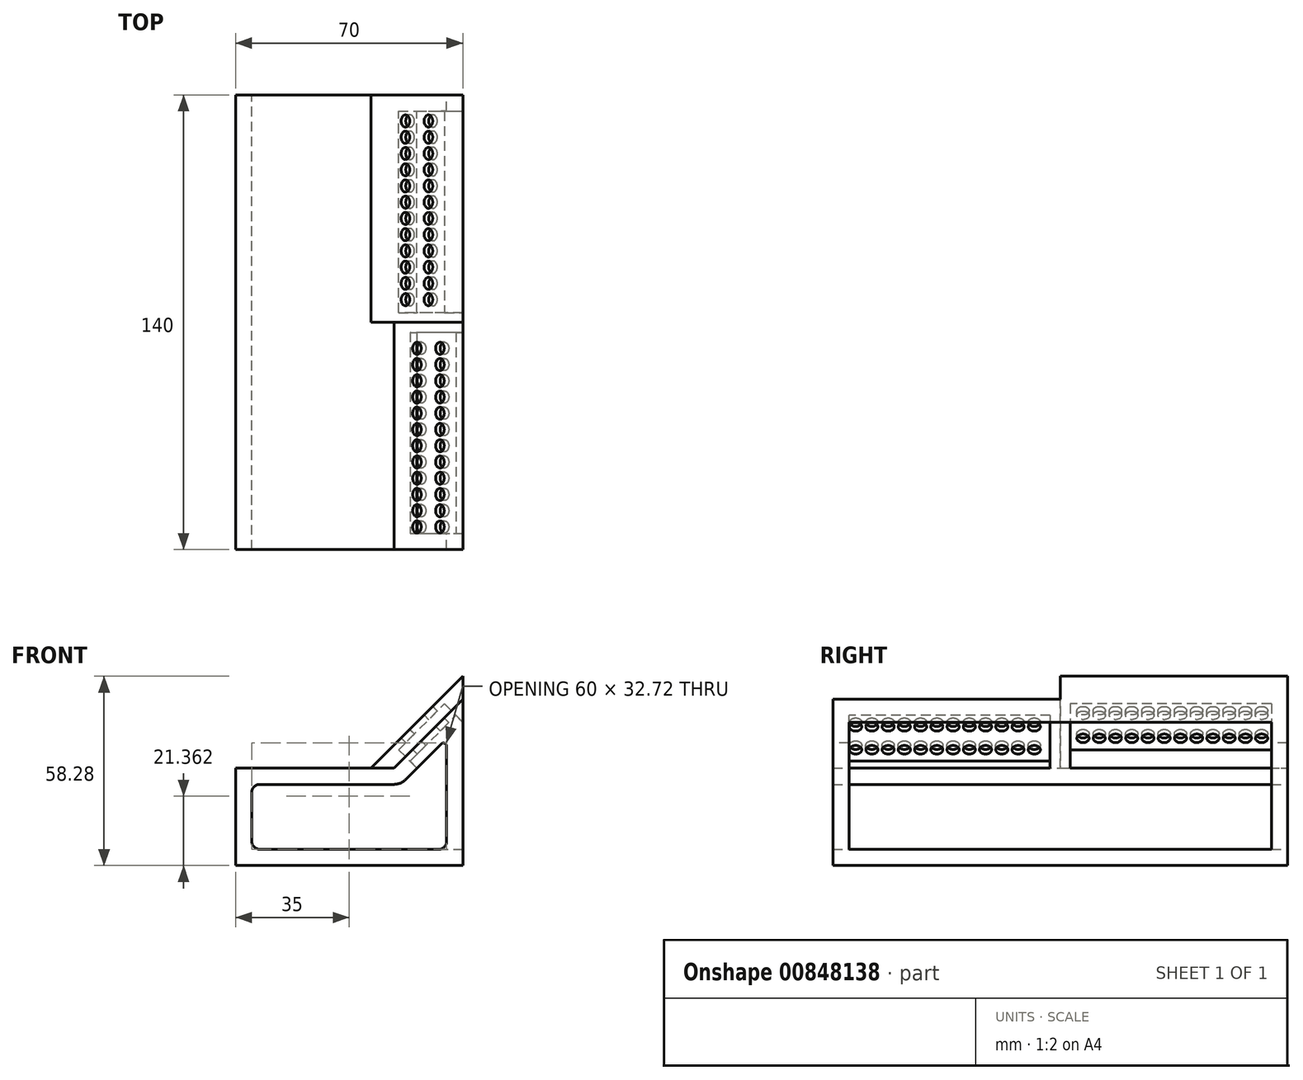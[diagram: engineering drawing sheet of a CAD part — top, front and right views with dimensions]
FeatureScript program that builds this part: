
annotation { "Feature Type Name" : "Feature", "Feature Type Description" : "" }
export const myFeature = defineFeature(function(context is Context, id is Id, definition is map)
    precondition{}
    {
        {
            var Q0;
            Q0=qCreatedBy(makeId("Front.planeOp"),FACE);
            var sketch = newSketch(context, id + "F0", { "sketchPlane" : qUnion([Q0])});
            skLineSegment(sketch, "E0.bottom", {"start": v(-35, 0) * mm, "end": v(35, 0) * mm});
            skLineSegment(sketch, "E0.top", {"start": v(-35, 30) * mm, "end": v(13.79, 30) * mm});
            skLineSegment(sketch, "E0.left", {"start": v(-35, 0) * mm, "end": v(-35, 30) * mm});
            skLineSegment(sketch, "E0.right", {"start": v(35, 0) * mm, "end": v(35, 30) * mm});
            skLineSegment(sketch, "E1", {"start": v(13.79, 30) * mm, "end": v(35, 51.21) * mm});
            skLineSegment(sketch, "E2", {"start": v(35, 51.21) * mm, "end": v(35, 30) * mm});
            skLineSegment(sketch, "E3.0", {"start": v(-30, 5) * mm, "end": v(-30, 25) * mm});
            skLineSegment(sketch, "E3.1", {"start": v(30, 5) * mm, "end": v(30, 30) * mm});
            skLineSegment(sketch, "E3.2", {"start": v(30, 39.14) * mm, "end": v(30, 30) * mm});
            skLineSegment(sketch, "E3.3", {"start": v(-30, 5) * mm, "end": v(30, 5) * mm});
            skLineSegment(sketch, "E3.4", {"start": v(15.86, 25) * mm, "end": v(30, 39.14) * mm});
            skLineSegment(sketch, "E3.5", {"start": v(-30, 25) * mm, "end": v(15.86, 25) * mm});
            skSolve(sketch);
        }
        {
            var Q0;
            Q0 = qSketchRegion(id + "F0", true);
            extrude(context, id + "F1", {"entities" : qUnion([Q0]), "endBound" : BoundingType.SYMMETRIC, "depth" : 140 * mm, "offsetDistance" : 25 * mm});
        }
        {
            var Q0;
            Q0=qCreatedBy(makeId("Front.planeOp"),FACE);
            var sketch = newSketch(context, id + "F2", { "sketchPlane" : qUnion([Q0])});
            skLineSegment(sketch, "E4", {"start": v(30, 39.14) * mm, "end": v(35, 44.14) * mm});
            skLineSegment(sketch, "E5", {"start": v(30, 39.14) * mm, "end": v(30, 5) * mm});
            skLineSegment(sketch, "E6", {"start": v(30, 5) * mm, "end": v(35, 5) * mm});
            skLineSegment(sketch, "E7", {"start": v(35, 5) * mm, "end": v(35, 44.14) * mm});
            skSolve(sketch);
        }
        {
            var Q0;
            Q0 = qSketchRegion(id + "F2", true);
            extrude(context, id + "F3", {"entities" : qUnion([Q0]), "operationType" : NewBodyOperationType.REMOVE, "endBound" : BoundingType.SYMMETRIC, "oppositeDirection" : true, "depth" : 130 * mm, "offsetDistance" : 25 * mm});
        }
        {
            var Q0;
            Q0=makeQuery(id+"F1.opExtrude","CAP_FACE",FACE,{"disambiguationData":[OSD([sQuery(id+"F0.wireOp",EDGE,"E0.bottom"),sQuery(id+"F0.wireOp",EDGE,"E0.top"),sQuery(id+"F0.wireOp",EDGE,"E0.left"),sQuery(id+"F0.wireOp",EDGE,"E0.right"),sQuery(id+"F0.wireOp",EDGE,"E1"),sQuery(id+"F0.wireOp",EDGE,"E2"),sQuery(id+"F0.wireOp",EDGE,"E3.0"),sQuery(id+"F0.wireOp",EDGE,"E3.1"),sQuery(id+"F0.wireOp",EDGE,"E3.2"),sQuery(id+"F0.wireOp",EDGE,"E3.3"),sQuery(id+"F0.wireOp",EDGE,"E3.4"),sQuery(id+"F0.wireOp",EDGE,"E3.5")])],"isStart":true});
            var sketch = newSketch(context, id + "F4", { "sketchPlane" : qUnion([Q0])});
            skLineSegment(sketch, "E8", {"start": v(-6.72, 30) * mm, "end": v(-13.79, 30) * mm});
            skLineSegment(sketch, "E9", {"start": v(-13.79, 30) * mm, "end": v(-35, 51.21) * mm});
            skLineSegment(sketch, "E10", {"start": v(-35, 51.21) * mm, "end": v(-35, 58.28) * mm});
            skLineSegment(sketch, "E11", {"start": v(-35, 58.28) * mm, "end": v(-6.72, 30) * mm});
            skSolve(sketch);
        }
        {
            var Q0;
            Q0 = qSketchRegion(id + "F4", true);
            extrude(context, id + "F5", {"entities" : qUnion([Q0]), "operationType" : NewBodyOperationType.ADD, "oppositeDirection" : true, "depth" : 70 * mm, "offsetDistance" : 25 * mm});
        }
        {
            var Q0;
            Q0=makeQuery(id+"F1.opExtrude","SWEPT_EDGE",EDGE,{"disambiguationData":[OSD([sQuery(id+"F0.wireOp",EDGE,"E3.0"),sQuery(id+"F0.wireOp",EDGE,"E3.3")])]});
            var Q1;
            Q1=makeQuery(id+"F1.opExtrude","SWEPT_EDGE",EDGE,{"disambiguationData":[OSD([sQuery(id+"F0.wireOp",EDGE,"E3.0"),sQuery(id+"F0.wireOp",EDGE,"E3.5")])]});
            var Q2;
            {var subQ0=sQuery(id+"F2.wireOp",EDGE,"E6");var subQ1=sQuery(id+"F0.wireOp",EDGE,"E3.3");var subQ3=sQuery(id+"F0.wireOp",EDGE,"E3.1");Q2=makeQuery(id+"F3.boolean.opBoolean","SPLIT",EDGE,{"disambiguationData":[TD([makeQuery(id+"F3.opExtrude","CAP_FACE",FACE,{"disambiguationData":[OSD([sQuery(id+"F2.wireOp",EDGE,"E4"),sQuery(id+"F2.wireOp",EDGE,"E5"),subQ0,sQuery(id+"F2.wireOp",EDGE,"E7")])],"isStart":true})])],"derivedFrom":makeQuery(id+"F1.opExtrude","SWEPT_EDGE",EDGE,{"disambiguationData":[OSD([subQ3,subQ1])]})});}
            var Q3;
            {var subQ0=sQuery(id+"F2.wireOp",EDGE,"E6");var subQ1=sQuery(id+"F0.wireOp",EDGE,"E3.3");var subQ3=sQuery(id+"F0.wireOp",EDGE,"E3.1");Q3=makeQuery(id+"F3.boolean.opBoolean","SPLIT",EDGE,{"disambiguationData":[TD([makeQuery(id+"F3.opExtrude","CAP_FACE",FACE,{"disambiguationData":[OSD([sQuery(id+"F2.wireOp",EDGE,"E4"),sQuery(id+"F2.wireOp",EDGE,"E5"),subQ0,sQuery(id+"F2.wireOp",EDGE,"E7")])],"isStart":false})])],"derivedFrom":makeQuery(id+"F1.opExtrude","SWEPT_EDGE",EDGE,{"disambiguationData":[OSD([subQ3,subQ1])]})});}
            fillet(context, id + "F6", {"entities" : qUnion([Q0, Q1, Q2, Q3]), "radius" : 2.5 * mm, "tangentPropagation" : true, "allowEdgeOverflow" : false});
        }
        {
            var Q0;
            Q0=makeQuery(id+"F1.opExtrude","SWEPT_EDGE",EDGE,{"disambiguationData":[OSD([sQuery(id+"F0.wireOp",EDGE,"E3.4"),sQuery(id+"F0.wireOp",EDGE,"E3.5")])]});
            fillet(context, id + "F7", {"entities" : qUnion([Q0]), "radius" : 5 * mm, "tangentPropagation" : true, "allowEdgeOverflow" : false});
        }
        {
            var Q0;
            {var subQ0=sQuery(id+"F0.wireOp",EDGE,"E3.4");var subQ1=sQuery(id+"F2.wireOp",EDGE,"E4");var subQ2=sQuery(id+"F0.wireOp",EDGE,"E3.2");Q0=makeQuery(id+"F3.boolean.opBoolean","SPLIT",EDGE,{"disambiguationData":[TD([makeQuery(id+"F3.opExtrude","CAP_FACE",FACE,{"disambiguationData":[OSD([subQ1,sQuery(id+"F2.wireOp",EDGE,"E5"),sQuery(id+"F2.wireOp",EDGE,"E6"),sQuery(id+"F2.wireOp",EDGE,"E7")])],"isStart":true})])],"derivedFrom":makeQuery(id+"F1.opExtrude","SWEPT_EDGE",EDGE,{"disambiguationData":[OSD([subQ2,subQ0])]})});}
            var Q1;
            {var subQ0=sQuery(id+"F0.wireOp",EDGE,"E3.4");var subQ1=sQuery(id+"F2.wireOp",EDGE,"E4");var subQ2=sQuery(id+"F0.wireOp",EDGE,"E3.2");Q1=makeQuery(id+"F3.boolean.opBoolean","SPLIT",EDGE,{"disambiguationData":[TD([makeQuery(id+"F3.opExtrude","CAP_FACE",FACE,{"disambiguationData":[OSD([subQ1,sQuery(id+"F2.wireOp",EDGE,"E5"),sQuery(id+"F2.wireOp",EDGE,"E6"),sQuery(id+"F2.wireOp",EDGE,"E7")])],"isStart":false})])],"derivedFrom":makeQuery(id+"F1.opExtrude","SWEPT_EDGE",EDGE,{"disambiguationData":[OSD([subQ2,subQ0])]})});}
            fillet(context, id + "F8", {"entities" : qUnion([Q0, Q1]), "radius" : 1 * mm, "tangentPropagation" : true, "allowEdgeOverflow" : false});
        }
        {
            var Q0;
            Q0=makeQuery(id+"F5.opExtrude","SWEPT_FACE",FACE,{"disambiguationData":[OSD([sQuery(id+"F4.wireOp",EDGE,"E11")])]});
            var sketch = newSketch(context, id + "F9", { "sketchPlane" : qUnion([Q0])});
            skCircle(sketch, "E12", {"center": v(-62, 50.96) * mm, "radius": 1.88 * mm});
            skLineSegment(sketch, "E13", {"start": v(-70, 45.96) * mm, "end": v(0, 45.96) * mm, "construction": true});
            skCircle(sketch, "E14.1.0.0", {"center": v(-57, 50.96) * mm, "radius": 1.88 * mm});
            skCircle(sketch, "E14.2.0.0", {"center": v(-52, 50.96) * mm, "radius": 1.88 * mm});
            skCircle(sketch, "E14.3.0.0", {"center": v(-47, 50.96) * mm, "radius": 1.88 * mm});
            skCircle(sketch, "E14.4.0.0", {"center": v(-42, 50.96) * mm, "radius": 1.88 * mm});
            skCircle(sketch, "E14.5.0.0", {"center": v(-37, 50.96) * mm, "radius": 1.88 * mm});
            skCircle(sketch, "E14.6.0.0", {"center": v(-32, 50.96) * mm, "radius": 1.88 * mm});
            skCircle(sketch, "E14.7.0.0", {"center": v(-27, 50.96) * mm, "radius": 1.88 * mm});
            skCircle(sketch, "E14.8.0.0", {"center": v(-22, 50.96) * mm, "radius": 1.88 * mm});
            skCircle(sketch, "E14.9.0.0", {"center": v(-17, 50.96) * mm, "radius": 1.88 * mm});
            skCircle(sketch, "E14.10.0.0", {"center": v(-12, 50.96) * mm, "radius": 1.88 * mm});
            skCircle(sketch, "E14.11.0.0", {"center": v(-7, 50.96) * mm, "radius": 1.88 * mm});
            skCircle(sketch, "E14.14.0.0", {"center": v(8, 50.96) * mm, "radius": 1.88 * mm});
            skCircle(sketch, "E14.15.0.0", {"center": v(13, 50.96) * mm, "radius": 1.88 * mm});
            skCircle(sketch, "E14.16.0.0", {"center": v(18, 50.96) * mm, "radius": 1.88 * mm});
            skCircle(sketch, "E14.17.0.0", {"center": v(23, 50.96) * mm, "radius": 1.88 * mm});
            skCircle(sketch, "E14.18.0.0", {"center": v(28, 50.96) * mm, "radius": 1.88 * mm});
            skCircle(sketch, "E14.19.0.0", {"center": v(33, 50.96) * mm, "radius": 1.88 * mm});
            skCircle(sketch, "E14.20.0.0", {"center": v(38, 50.96) * mm, "radius": 1.88 * mm});
            skCircle(sketch, "E14.21.0.0", {"center": v(43, 50.96) * mm, "radius": 1.88 * mm});
            skCircle(sketch, "E14.22.0.0", {"center": v(48, 50.96) * mm, "radius": 1.88 * mm});
            skCircle(sketch, "E14.23.0.0", {"center": v(53, 50.96) * mm, "radius": 1.88 * mm});
            skCircle(sketch, "E14.24.0.0", {"center": v(58, 50.96) * mm, "radius": 1.88 * mm});
            skCircle(sketch, "E14.25.0.0", {"center": v(63, 50.96) * mm, "radius": 1.88 * mm});
            skLineSegment(sketch, "E14.direction1", {"start": v(-62, 50.96) * mm, "end": v(-57, 50.96) * mm, "construction": true});
            skCircle(sketch, "E15.MirrorC", {"center": v(-62, 40.96) * mm, "radius": 1.88 * mm});
            skCircle(sketch, "E16.MirrorC", {"center": v(-57, 40.96) * mm, "radius": 1.88 * mm});
            skCircle(sketch, "E17.MirrorC", {"center": v(-52, 40.96) * mm, "radius": 1.88 * mm});
            skCircle(sketch, "E18.MirrorC", {"center": v(-47, 40.96) * mm, "radius": 1.88 * mm});
            skCircle(sketch, "E19.MirrorC", {"center": v(-42, 40.96) * mm, "radius": 1.88 * mm});
            skCircle(sketch, "E20.MirrorC", {"center": v(-37, 40.96) * mm, "radius": 1.88 * mm});
            skCircle(sketch, "E21.MirrorC", {"center": v(-32, 40.96) * mm, "radius": 1.88 * mm});
            skCircle(sketch, "E22.MirrorC", {"center": v(-27, 40.96) * mm, "radius": 1.88 * mm});
            skCircle(sketch, "E23.MirrorC", {"center": v(-22, 40.96) * mm, "radius": 1.88 * mm});
            skCircle(sketch, "E24.MirrorC", {"center": v(-17, 40.96) * mm, "radius": 1.88 * mm});
            skCircle(sketch, "E25.MirrorC", {"center": v(-12, 40.96) * mm, "radius": 1.88 * mm});
            skCircle(sketch, "E26.MirrorC", {"center": v(-7, 40.96) * mm, "radius": 1.88 * mm});
            skCircle(sketch, "E27.MirrorC", {"center": v(8, 40.96) * mm, "radius": 1.88 * mm});
            skCircle(sketch, "E28.MirrorC", {"center": v(13, 40.96) * mm, "radius": 1.88 * mm});
            skCircle(sketch, "E29.MirrorC", {"center": v(18, 40.96) * mm, "radius": 1.88 * mm});
            skCircle(sketch, "E30.MirrorC", {"center": v(23, 40.96) * mm, "radius": 1.88 * mm});
            skCircle(sketch, "E31.MirrorC", {"center": v(28, 40.96) * mm, "radius": 1.88 * mm});
            skCircle(sketch, "E32.MirrorC", {"center": v(33, 40.96) * mm, "radius": 1.88 * mm});
            skCircle(sketch, "E33.MirrorC", {"center": v(38, 40.96) * mm, "radius": 1.88 * mm});
            skCircle(sketch, "E34.MirrorC", {"center": v(43, 40.96) * mm, "radius": 1.88 * mm});
            skCircle(sketch, "E35.MirrorC", {"center": v(48, 40.96) * mm, "radius": 1.88 * mm});
            skCircle(sketch, "E36.MirrorC", {"center": v(53, 40.96) * mm, "radius": 1.88 * mm});
            skCircle(sketch, "E37.MirrorC", {"center": v(58, 40.96) * mm, "radius": 1.88 * mm});
            skCircle(sketch, "E38.MirrorC", {"center": v(63, 40.96) * mm, "radius": 1.88 * mm});
            skSolve(sketch);
        }
        {
            var Q0;
            Q0 = qSketchRegion(id + "F9", true);
            extrude(context, id + "F10", {"entities" : qUnion([Q0]), "operationType" : NewBodyOperationType.REMOVE, "endBound" : BoundingType.THROUGH_ALL, "oppositeDirection" : true, "depth" : 25 * mm, "offsetDistance" : 25 * mm});
        }
        {
            var Q0;
            Q0=makeQuery(id+"F3.boolean.opBoolean","MERGE",FACE,{"derivedFrom":[makeQuery(id+"F1.opExtrude","SWEPT_FACE",FACE,{"disambiguationData":[OSD([sQuery(id+"F0.wireOp",EDGE,"E3.4")])]}),makeQuery(id+"F3.opExtrude","SWEPT_FACE",FACE,{"disambiguationData":[OSD([sQuery(id+"F2.wireOp",EDGE,"E4")])]})]});
            var sketch = newSketch(context, id + "F11", { "sketchPlane" : qUnion([Q0])});
            skLineSegment(sketch, "E39", {"start": v(-3.12, 35.96) * mm, "end": v(-65, 35.96) * mm});
            skLineSegment(sketch, "E40", {"start": v(-65, 35.96) * mm, "end": v(-65, 55.96) * mm});
            skLineSegment(sketch, "E41", {"start": v(-65, 55.96) * mm, "end": v(-3.12, 55.96) * mm});
            skLineSegment(sketch, "E42", {"start": v(-3.12, 55.96) * mm, "end": v(-3.12, 35.96) * mm});
            skSolve(sketch);
        }
        {
            var Q0;
            Q0 = qSketchRegion(id + "F11", true);
            extrude(context, id + "F12", {"entities" : qUnion([Q0]), "operationType" : NewBodyOperationType.REMOVE, "oppositeDirection" : true, "depth" : 3 * mm, "offsetDistance" : 25 * mm});
        }
        {
            var Q0;
            Q0=makeQuery(id+"F3.boolean.opBoolean","MERGE",FACE,{"derivedFrom":[makeQuery(id+"F1.opExtrude","SWEPT_FACE",FACE,{"disambiguationData":[OSD([sQuery(id+"F0.wireOp",EDGE,"E3.4")])]}),makeQuery(id+"F3.opExtrude","SWEPT_FACE",FACE,{"disambiguationData":[OSD([sQuery(id+"F2.wireOp",EDGE,"E4")])]})]});
            var sketch = newSketch(context, id + "F13", { "sketchPlane" : qUnion([Q0])});
            skLineSegment(sketch, "E43", {"start": v(3, 55.96) * mm, "end": v(3, 35.96) * mm});
            skLineSegment(sketch, "E44", {"start": v(3, 35.96) * mm, "end": v(65, 35.96) * mm});
            skLineSegment(sketch, "E45", {"start": v(65, 35.96) * mm, "end": v(65, 55.96) * mm});
            skLineSegment(sketch, "E46", {"start": v(65, 55.96) * mm, "end": v(3, 55.96) * mm});
            skSolve(sketch);
        }
        {
            var Q0;
            Q0=makeQuery(id+"F13.imprint","IMPRINT",FACE,{"disambiguationData":[TD([[makeQuery(id+"F13.imprint","IMPRINT",EDGE,{"derivedFrom":sQuery(id+"F13.wireOp",EDGE,"E43")}),1.0]])]});
            extrude(context, id + "F14", {"entities" : qUnion([Q0]), "operationType" : NewBodyOperationType.REMOVE, "oppositeDirection" : true, "depth" : 8 * mm, "offsetDistance" : 25 * mm});
        }
    });
